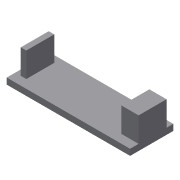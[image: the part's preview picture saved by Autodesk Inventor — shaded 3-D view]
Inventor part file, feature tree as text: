
AUTODESK INVENTOR PART (.ipt)
format: ipt  version: 2019.4 (Build 234330000, 330)  size: 86,016 bytes
history: native  units: mm
features: extrude x2, sketch x2
ambient origin geometry x8: Origin, YZ Plane, XZ Plane, XY Plane, X Axis, Y Axis, Z Axis, Center Point
bodies: Solid1 (feature_tree)
feature tree (4):
  extrude  "Extrusion1"  Depth=14.0mm
  extrude  "Extrusion2"  Depth=8.0mm TaperAngle=0.0deg
  sketch  "Sketch1"  dims[d0=40.0mm d1=14.0mm]
  sketch  "Sketch2"  dims[d2=2.0mm d3=0.0mm d4=8.0mm d5=0.0mm]
